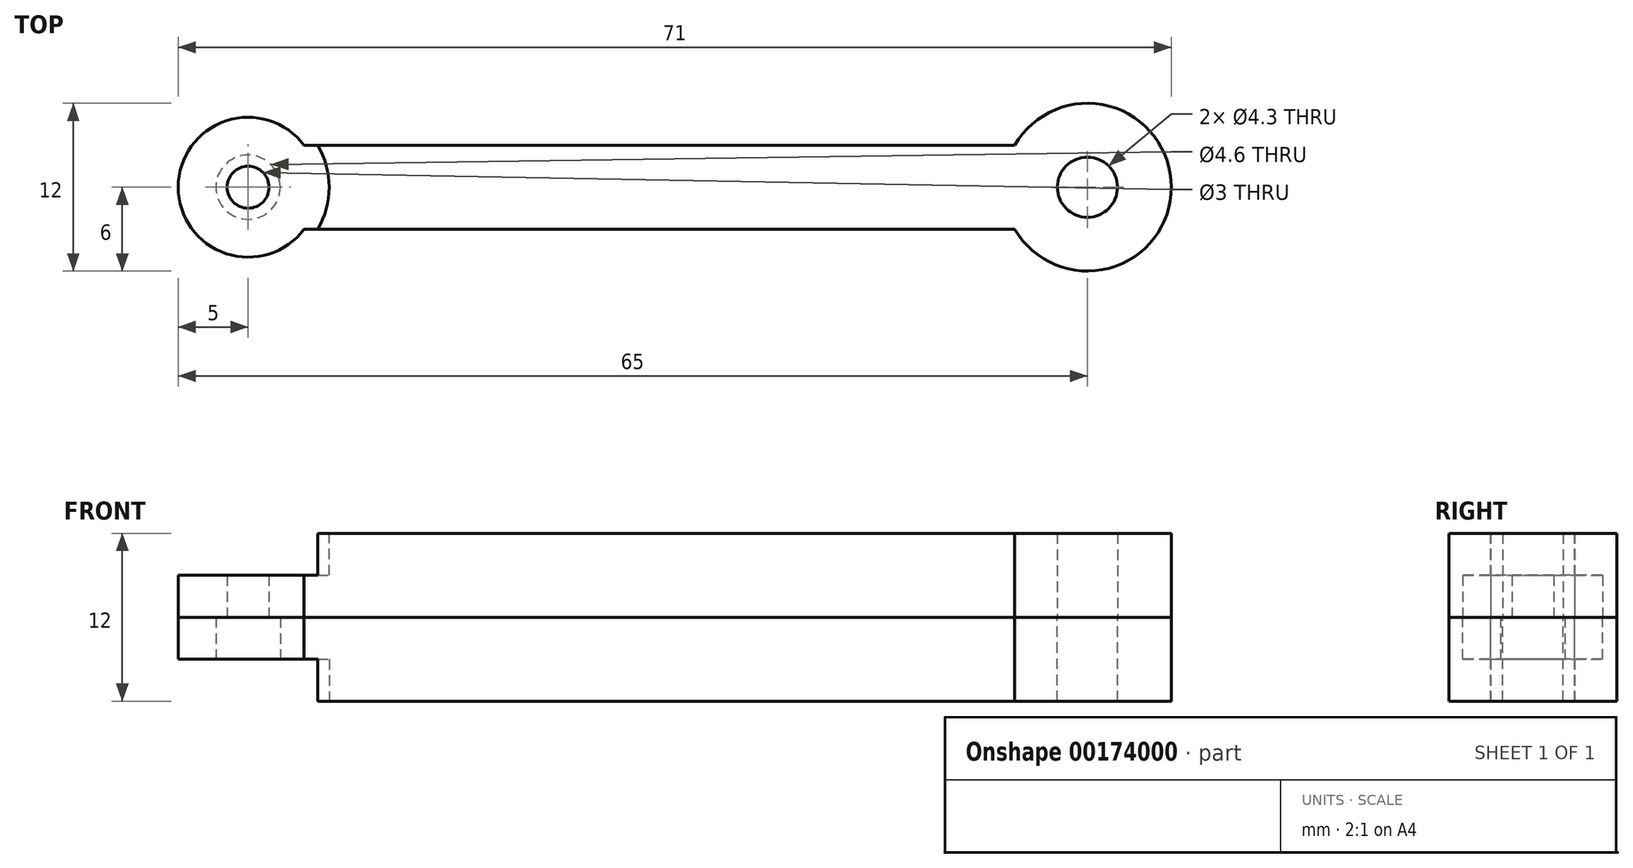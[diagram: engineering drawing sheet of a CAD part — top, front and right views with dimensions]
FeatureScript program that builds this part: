
annotation { "Feature Type Name" : "Feature", "Feature Type Description" : "" }
export const myFeature = defineFeature(function(context is Context, id is Id, definition is map)
    precondition{}
    {
        {
            var Q0;
            Q0=qCreatedBy(makeId("Top.planeOp"),FACE);
            var sketch = newSketch(context, id + "F0", { "sketchPlane" : qUnion([Q0])});
            skCircle(sketch, "E0", {"center": v(0, 0) * mm, "radius": 2.15 * mm});
            skCircle(sketch, "E1", {"center": v(0, 0) * mm, "radius": 6 * mm});
            skLineSegment(sketch, "E2", {"start": v(-5.2, 3) * mm, "end": v(-56, 3) * mm});
            skLineSegment(sketch, "E3", {"start": v(-5.2, -3) * mm, "end": v(-56, -3) * mm});
            skCircle(sketch, "E4", {"center": v(-60, 0) * mm, "radius": 1.5 * mm});
            skCircle(sketch, "E5", {"center": v(-60, 0) * mm, "radius": 5 * mm});
            skSolve(sketch);
        }
        {
            var Q0;
            Q0 = qSketchRegion(id + "F0", true);
            extrude(context, id + "F1", {"entities" : qUnion([Q0]), "depth" : 6 * mm});
        }
        {
            var Q0;
            Q0=makeQuery(id+"F1.opExtrude","CAP_FACE",FACE,{"disambiguationData":[OSD([sQuery(id+"F0.wireOp",EDGE,"E0"),sQuery(id+"F0.wireOp",EDGE,"E1"),sQuery(id+"F0.wireOp",EDGE,"E2"),sQuery(id+"F0.wireOp",EDGE,"E3"),sQuery(id+"F0.wireOp",EDGE,"E4"),sQuery(id+"F0.wireOp",EDGE,"E5")])],"isStart":false});
            var sketch = newSketch(context, id + "F2", { "sketchPlane" : qUnion([Q0])});
            skCircle(sketch, "E6", {"center": v(-60, 0) * mm, "radius": 5.8 * mm});
            skSolve(sketch);
        }
        {
            var Q0;
            Q0 = qSketchRegion(id + "F2", true);
            extrude(context, id + "F3", {"entities" : qUnion([Q0]), "operationType" : NewBodyOperationType.REMOVE, "oppositeDirection" : true, "depth" : 3 * mm});
        }
        {
            var Q0;
            Q0=makeQuery(id+"F1.opExtrude","SWEPT_BODY",BODY,{"disambiguationData":[OSD([sQuery(id+"F0.wireOp",EDGE,"E0"),sQuery(id+"F0.wireOp",EDGE,"E1"),sQuery(id+"F0.wireOp",EDGE,"E2"),sQuery(id+"F0.wireOp",EDGE,"E3"),sQuery(id+"F0.wireOp",EDGE,"E4"),sQuery(id+"F0.wireOp",EDGE,"E5")])]});
            var Q1;
            Q1=makeQuery(id+"F1.opExtrude","CAP_FACE",FACE,{"disambiguationData":[OSD([sQuery(id+"F0.wireOp",EDGE,"E0"),sQuery(id+"F0.wireOp",EDGE,"E1"),sQuery(id+"F0.wireOp",EDGE,"E2"),sQuery(id+"F0.wireOp",EDGE,"E3"),sQuery(id+"F0.wireOp",EDGE,"E4"),sQuery(id+"F0.wireOp",EDGE,"E5")])],"isStart":true});
            mirror(context, id + "F4", {"entities" : qUnion([Q0]), "mirrorPlane" : qUnion([Q1])});
        }
        {
            var Q0;
            Q0=makeQuery(id+"F4.opPattern","COPY",FACE,{"derivedFrom":makeQuery(id+"F3.boolean.opBoolean","COPY",FACE,{"derivedFrom":makeQuery(id+"F3.opExtrude","CAP_FACE",FACE,{"disambiguationData":[OSD([sQuery(id+"F2.wireOp",EDGE,"E6")])],"isStart":false})}),"instanceName":"1"});
            var sketch = newSketch(context, id + "F5", { "sketchPlane" : qUnion([Q0])});
            skCircle(sketch, "E7", {"center": v(-60, 0) * mm, "radius": 2.3 * mm});
            skSolve(sketch);
        }
        {
            var Q0;
            Q0 = qSketchRegion(id + "F5", true);
            var Q1;
            Q1=makeQuery(id+"F4.opPattern","COPY",FACE,{"derivedFrom":makeQuery(id+"F1.opExtrude","CAP_FACE",FACE,{"disambiguationData":[OSD([sQuery(id+"F0.wireOp",EDGE,"E0"),sQuery(id+"F0.wireOp",EDGE,"E1"),sQuery(id+"F0.wireOp",EDGE,"E2"),sQuery(id+"F0.wireOp",EDGE,"E3"),sQuery(id+"F0.wireOp",EDGE,"E4"),sQuery(id+"F0.wireOp",EDGE,"E5")])],"isStart":true}),"instanceName":"1"});
            extrude(context, id + "F6", {"entities" : qUnion([Q0]), "operationType" : NewBodyOperationType.REMOVE, "endBound" : BoundingType.UP_TO_SURFACE, "oppositeDirection" : true, "endBoundEntityFace" : qUnion([Q1]), "depth" : 25 * mm});
        }
    });
